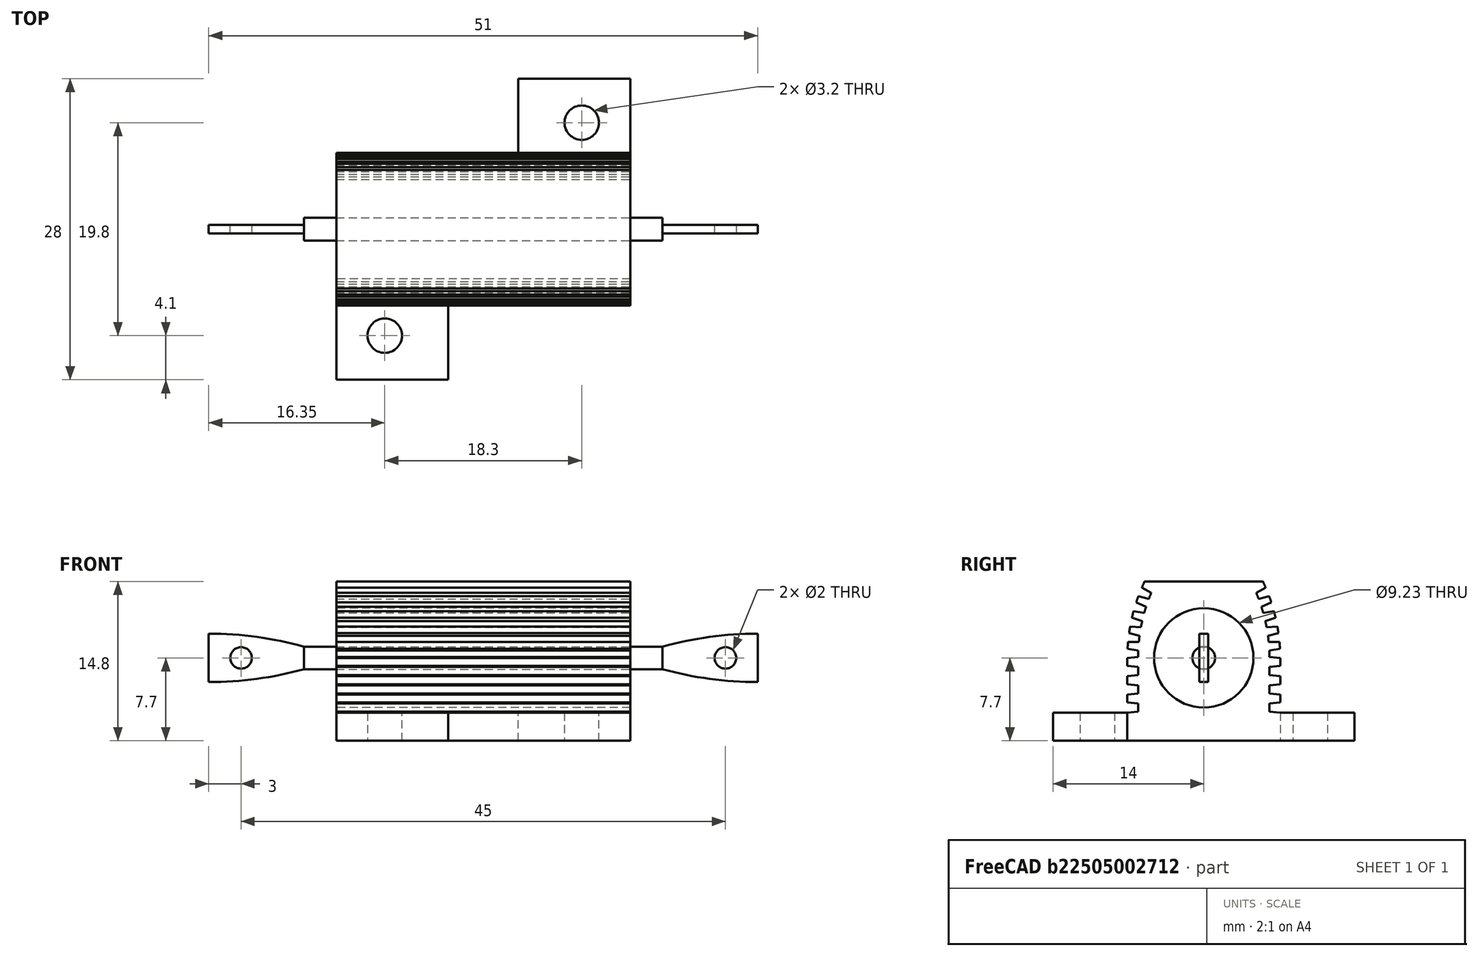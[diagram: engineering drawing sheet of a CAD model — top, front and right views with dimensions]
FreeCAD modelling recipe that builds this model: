
FCSTD DOCUMENT  (FreeCAD 0.20R29410 (Git))
Label: Arcol_HS10-50
License: All rights reserved
LicenseURL: http://en.wikipedia.org/wiki/All_rights_reserved
objects: Sketcher::SketchObject×5, Part::Extrusion×3, Part::Revolution×2, Spreadsheet::Sheet×1, Part::MultiFuse×1, Part::Compound×1
note: 12 computed .brp shape members not serialized (recipe doc carries the construction recipe); baked Part::Feature solids carry a one-line shape summary decoded from their .brp

FEATURE [Spreadsheet::Sheet] Spreadsheet  label="DS"
  cells = A1=A; B1(DS_A)=28; D1=16.5; E1=21; F1=28; G1=28; A2=B; B2(DS_B)=51; D2=30; E2=36.5; F2=51; G2=72.5; A3=C; B3(DS_C)=14.8; D3=8.800000000000001; E3=11; F3=14.8; G3=14.8; A4=D; B4(DS_D)=14.2; D4=8.5; E4=11.2; F4=14.2; G4=14.2; A5=E; B5(DS_E)=27.3; D5=15.9; E5=19.9; F5=27.3; G5=49.1; A6=F; B6(DS_F)=18.3; D6=11.3; E6=14.3; F6=18.3; G6=39.7; A7=G; B7(DS_G)=19.8; D7=12.4; E7=15.9; F7=19.8; G7=21.4; A8=H; B8(DS_H)=7.7; D8=4.5; E8=5.5; F8=7.7; G8=8.4; A9=J; B9(DS_J)=5.2; D9=2.4; E9=2.8; F9=5.2; G9=5.2; A10=K; B10(DS_K)=2.6; D10=1.8; E10=1.8; F10=2.6; G10=2.6; A11=L; B11(DS_L)=3.2; D11=2.4; E11=2.4; F11=3.2; G11=3.2; D13=HS10; E13=HS15; F13=HS25; G13=HS50; A14=Fill_Factor; B14(Fill_Factor)=0.65; A15=Fill_Cone_Height; B15(Fill_Cone_Height)=1; A16=Fill_Cone_Diam; B16(Fill_Cone_Size)=0.65; A17=Fin_Depth; B17(Fin_Depth)=1; A18=Fin_Draft; B18(Fin_Draft)=0.1; A19=Label_Width; B19(Label_Width)=11; A20=Wire_Diam; B20(Wire_Diam)=2.1; A21=Wire_Len; B21(Wire_Len)=3; A22=Con_Thickness; B22(Con_Thickness)=0.8; A23=Con_Width; B23(Con_Width)=4.5; A24=Con_Hole; B24(Con_Hole)=2; A25=Con_Hole_Dist; B25(Con_Hole_Dist)=3
FEATURE [Sketcher::SketchObject] Sketch  label="Sketch_Body_Main"
  FullyConstrained = true
  Placement = pos=(0,0,0) rot=(0.57735,0.57735,0.57735;2.0944rad)
  expr: Constraints[157] = <<DS>>.DS_K
  expr: Constraints[158] = <<DS>>.Fin_Draft
  expr: Constraints[159] = <<DS>>.Fin_Draft
  expr: Constraints[160] = <<DS>>.Fin_Draft
  expr: Constraints[161] = <<DS>>.Fin_Draft
  expr: Constraints[162] = <<DS>>.Fin_Draft
  expr: Constraints[163] = <<DS>>.Fin_Draft
  expr: Constraints[1] = <<DS>>.Label_Width / 2
  expr: Constraints[233] = <<DS>>.DS_D * <<DS>>.Fill_Factor
  expr: Constraints[234] = <<DS>>.DS_H
  expr: Constraints[236] = <<DS>>.Fin_Draft
  expr: Constraints[239] = <<DS>>.Fin_Draft
  expr: Constraints[2] = <<DS>>.DS_C
  expr: Constraints[46] = <<DS>>.Fin_Draft
  expr: Constraints[47] = <<DS>>.Fin_Draft
  expr: Constraints[48] = <<DS>>.Fin_Draft
  expr: Constraints[49] = <<DS>>.Fin_Draft
  expr: Constraints[50] = <<DS>>.Fin_Draft
  expr: Constraints[51] = <<DS>>.Fin_Draft
  expr: Constraints[52] = <<DS>>.Fin_Draft
  expr: Constraints[53] = <<DS>>.Fin_Draft
  expr: Constraints[5] = <<DS>>.DS_D / 2
  expr: Constraints[6] = <<DS>>.DS_H
  expr: Constraints[9] = <<DS>>.Fin_Depth
  sketch-geometry (100):
    g0: LineSegment StartX=-5.5 StartY=14.8 StartZ=0 EndX=5.5 EndY=14.8 EndZ=0
    g1: ArcOfCircle CenterX=-9.45313 CenterY=7.7 CenterZ=0 NormalX=0 NormalY=0 NormalZ=1 AngleXU=0 Radius=16.5531 StartAngle=0 EndAngle=0.443299
    g2: ArcOfCircle CenterX=-9.45313 CenterY=7.7 CenterZ=0 NormalX=0 NormalY=0 NormalZ=1 AngleXU=0 Radius=15.5531 StartAngle=0 EndAngle=0.917514
    g3: LineSegment StartX=-9.45313 StartY=7.7 StartZ=0 EndX=7.0997 EndY=7.8 EndZ=0
    g4: LineSegment StartX=-9.45313 StartY=7.7 StartZ=0 EndX=7.08374 EndY=8.43356 EndZ=0
    g5: LineSegment StartX=-9.45313 StartY=7.7 StartZ=0 EndX=7.079 EndY=8.53345 EndZ=0
    g6: LineSegment StartX=7.03498 StartY=9.16568 StartZ=0 EndX=-9.45313 EndY=7.7 EndZ=0
    g7: LineSegment StartX=-9.45313 StartY=7.7 StartZ=0 EndX=7.02583 EndY=9.26526 EndZ=0
    g8: LineSegment StartX=6.95383 StartY=9.89491 StartZ=0 EndX=-9.45313 EndY=7.7 EndZ=0
    g9: LineSegment StartX=-9.45313 StartY=7.7 StartZ=0 EndX=6.94027 EndY=9.99399 EndZ=0
    g10: LineSegment StartX=6.84045 StartY=10.6198 StartZ=0 EndX=-9.45313 EndY=7.7 EndZ=0
    g11: LineSegment StartX=6.82251 StartY=10.7182 StartZ=0 EndX=-9.45313 EndY=7.7 EndZ=0
    g12: LineSegment StartX=6.67277 StartY=11.4365 StartZ=0 EndX=-9.45313 EndY=7.7 EndZ=0
    g13: LineSegment StartX=6.69505 StartY=11.339 StartZ=0 EndX=-9.45313 EndY=7.7 EndZ=0
    g14: LineSegment StartX=6.51792 StartY=12.0511 StartZ=0 EndX=-9.45313 EndY=7.7 EndZ=0
    g15: LineSegment StartX=6.49134 StartY=12.1475 StartZ=0 EndX=-9.45313 EndY=7.7 EndZ=0
    g16: LineSegment StartX=6.30941 StartY=12.7546 StartZ=0 EndX=-9.45313 EndY=7.7 EndZ=0
    g17: LineSegment StartX=6.27859 StartY=12.8497 StartZ=0 EndX=-9.45313 EndY=7.7 EndZ=0
    g18: LineSegment StartX=6.03492 StartY=13.5418 StartZ=0 EndX=-9.45313 EndY=7.7 EndZ=0
    g19: LineSegment StartX=6.06993 StartY=13.4481 StartZ=0 EndX=-9.45313 EndY=7.7 EndZ=0
    g20: LineSegment StartX=5.79995 StartY=14.1304 StartZ=0 EndX=-9.45313 EndY=7.7 EndZ=0
    g21: LineSegment StartX=6.30941 StartY=12.7546 StartZ=0 EndX=6.49134 EndY=12.1475 EndZ=0
    g22: LineSegment StartX=6.84045 StartY=10.6198 StartZ=0 EndX=6.94027 EndY=9.99399 EndZ=0
    g23: LineSegment StartX=6.95383 StartY=9.89491 StartZ=0 EndX=7.02583 EndY=9.26526 EndZ=0
    g24: LineSegment StartX=7.03498 StartY=9.16568 StartZ=0 EndX=7.079 EndY=8.53345 EndZ=0
    g25: LineSegment StartX=7.08374 StartY=8.43356 StartZ=0 EndX=7.0997 EndY=7.8 EndZ=0
    g26: LineSegment StartX=7.1 StartY=7.7 StartZ=0 EndX=6.09972 EndY=7.79396 EndZ=0
    g27: LineSegment StartX=6.08472 StartY=8.38924 StartZ=0 EndX=7.079 EndY=8.53345 EndZ=0
    g28: LineSegment StartX=7.03498 StartY=9.16568 StartZ=0 EndX=6.03031 EndY=9.1707 EndZ=0
    g29: LineSegment StartX=5.96266 StartY=9.76231 StartZ=0 EndX=6.94027 EndY=9.99399 EndZ=0
    g30: LineSegment StartX=6.84045 StartY=10.6198 StartZ=0 EndX=5.83927 EndY=10.5359 EndZ=0
    g31: LineSegment StartX=5.71951 StartY=11.1192 StartZ=0 EndX=6.67277 EndY=11.4365 EndZ=0
    g32: LineSegment StartX=6.51792 StartY=12.0511 StartZ=0 EndX=5.52811 EndY=11.8788 EndZ=0
    g33: LineSegment StartX=5.35717 StartY=12.4492 StartZ=0 EndX=6.27859 EndY=12.8497 EndZ=0
    g34: LineSegment StartX=6.06993 StartY=13.4481 StartZ=0 EndX=5.09926 EndY=13.1889 EndZ=0
    g35: ArcOfCircle CenterX=-9.45313 CenterY=7.7 CenterZ=0 NormalX=0 NormalY=0 NormalZ=1 AngleXU=0 Radius=15.5531 StartAngle=0.00604116 EndAngle=0.0443299
    g36: ArcOfCircle CenterX=-9.45313 CenterY=7.7 CenterZ=0 NormalX=0 NormalY=0 NormalZ=1 AngleXU=0 Radius=16.5531 StartAngle=0.0503711 EndAngle=0.0886598
    g37: ArcOfCircle CenterX=-9.45313 CenterY=7.7 CenterZ=0 NormalX=0 NormalY=0 NormalZ=1 AngleXU=0 Radius=15.5531 StartAngle=0.094701 EndAngle=0.13299
    g38: ArcOfCircle CenterX=-9.45313 CenterY=7.7 CenterZ=0 NormalX=0 NormalY=0 NormalZ=1 AngleXU=0 Radius=16.5531 StartAngle=0.139031 EndAngle=0.17732
    g39: ArcOfCircle CenterX=-9.45313 CenterY=7.7 CenterZ=0 NormalX=0 NormalY=0 NormalZ=1 AngleXU=0 Radius=15.5531 StartAngle=0.183361 EndAngle=0.22165
    g40: ArcOfCircle CenterX=-9.45313 CenterY=7.7 CenterZ=0 NormalX=0 NormalY=0 NormalZ=1 AngleXU=0 Radius=16.5531 StartAngle=0.227691 EndAngle=0.265979
    g41: ArcOfCircle CenterX=-9.45313 CenterY=7.7 CenterZ=0 NormalX=0 NormalY=0 NormalZ=1 AngleXU=0 Radius=15.5531 StartAngle=0.272021 EndAngle=0.310309
    g42: ArcOfCircle CenterX=-9.45313 CenterY=7.7 CenterZ=0 NormalX=0 NormalY=0 NormalZ=1 AngleXU=0 Radius=16.5531 StartAngle=0.316351 EndAngle=0.354639
    g43: ArcOfCircle CenterX=-9.45313 CenterY=7.7 CenterZ=0 NormalX=0 NormalY=0 NormalZ=1 AngleXU=0 Radius=15.5531 StartAngle=0.36068 EndAngle=0.398969
    g44: LineSegment StartX=7.1 StartY=7.7 StartZ=0 EndX=7.1 EndY=6.95 EndZ=0
    g45: LineSegment StartX=7.1 StartY=6.95 StartZ=0 EndX=6.1 EndY=6.85 EndZ=0
    g46: LineSegment StartX=6.1 StartY=6.85 StartZ=0 EndX=6.1 EndY=6.1 EndZ=0
    g47: LineSegment StartX=6.1 StartY=6.1 StartZ=0 EndX=7.1 EndY=6 EndZ=0
    g48: LineSegment StartX=7.1 StartY=6 StartZ=0 EndX=7.1 EndY=5.25 EndZ=0
    g49: LineSegment StartX=7.1 StartY=5.25 StartZ=0 EndX=6.1 EndY=5.15 EndZ=0
    g50: LineSegment StartX=6.1 StartY=5.15 StartZ=0 EndX=6.1 EndY=4.4 EndZ=0
    g51: LineSegment StartX=6.1 StartY=4.4 StartZ=0 EndX=7.1 EndY=4.3 EndZ=0
    g52: LineSegment StartX=7.1 StartY=4.3 StartZ=0 EndX=7.1 EndY=3.55 EndZ=0
    g53: LineSegment StartX=7.1 StartY=3.55 StartZ=0 EndX=6.1 EndY=3.45 EndZ=0
    g54: LineSegment StartX=6.1 StartY=3.45 StartZ=0 EndX=6.1 EndY=2.7 EndZ=0
    g55: LineSegment StartX=6.1 StartY=2.7 StartZ=0 EndX=7.1 EndY=2.6 EndZ=0
    g56: LineSegment StartX=7.1 StartY=2.6 StartZ=0 EndX=7.1 EndY=0 EndZ=0
    g57: LineSegment StartX=7.1 StartY=0 StartZ=0 EndX=-7.1 EndY=0 EndZ=0
    g58: LineSegment StartX=-7.1 StartY=0 StartZ=0 EndX=-7.1 EndY=2.6 EndZ=0
    g59: LineSegment StartX=-7.1 StartY=2.6 StartZ=0 EndX=-6.1 EndY=2.7 EndZ=0
    g60: LineSegment StartX=-6.1 StartY=2.7 StartZ=0 EndX=-6.1 EndY=3.45 EndZ=0
    g61: LineSegment StartX=-6.1 StartY=3.45 StartZ=0 EndX=-7.1 EndY=3.55 EndZ=0
    g62: LineSegment StartX=-7.1 StartY=3.55 StartZ=0 EndX=-7.1 EndY=4.3 EndZ=0
    g63: LineSegment StartX=-7.1 StartY=4.3 StartZ=0 EndX=-6.1 EndY=4.4 EndZ=0
    g64: LineSegment StartX=-6.1 StartY=4.4 StartZ=0 EndX=-6.1 EndY=5.15 EndZ=0
    g65: LineSegment StartX=-6.1 StartY=5.15 StartZ=0 EndX=-7.1 EndY=5.25 EndZ=0
    g66: LineSegment StartX=-7.1 StartY=5.25 StartZ=0 EndX=-7.1 EndY=6 EndZ=0
    g67: LineSegment StartX=-7.1 StartY=6 StartZ=0 EndX=-6.1 EndY=6.1 EndZ=0
    g68: LineSegment StartX=-6.1 StartY=6.1 StartZ=0 EndX=-6.1 EndY=6.85 EndZ=0
    g69: LineSegment StartX=-6.1 StartY=6.85 StartZ=0 EndX=-7.1 EndY=6.95 EndZ=0
    g70: LineSegment StartX=-7.1 StartY=6.95 StartZ=0 EndX=-7.1 EndY=7.7 EndZ=0
    g71: LineSegment StartX=-7.1 StartY=7.7 StartZ=0 EndX=-6.09972 EndY=7.79396 EndZ=0
    g72: LineSegment StartX=-6.08472 StartY=8.38924 StartZ=0 EndX=-7.079 EndY=8.53345 EndZ=0
    g73: LineSegment StartX=-7.03498 StartY=9.16568 StartZ=0 EndX=-6.03031 EndY=9.1707 EndZ=0
    g74: LineSegment StartX=-5.96266 StartY=9.76231 StartZ=0 EndX=-6.94027 EndY=9.99399 EndZ=0
    g75: LineSegment StartX=-6.84045 StartY=10.6198 StartZ=0 EndX=-5.83927 EndY=10.5359 EndZ=0
    g76: LineSegment StartX=-5.71951 StartY=11.1192 StartZ=0 EndX=-6.67277 EndY=11.4365 EndZ=0
    g77: LineSegment StartX=-6.51792 StartY=12.0511 StartZ=0 EndX=-5.52811 EndY=11.8788 EndZ=0
    g78: LineSegment StartX=-5.35717 StartY=12.4492 StartZ=0 EndX=-6.27859 EndY=12.8497 EndZ=0
    g79: LineSegment StartX=-6.06993 StartY=13.4481 StartZ=0 EndX=-5.09926 EndY=13.1889 EndZ=0
    g80: ArcOfCircle CenterX=9.45313 CenterY=7.7 CenterZ=0 NormalX=0 NormalY=0 NormalZ=1 AngleXU=0 Radius=15.5531 StartAngle=3.09726 EndAngle=3.13555
    g81: ArcOfCircle CenterX=9.45313 CenterY=7.7 CenterZ=0 NormalX=0 NormalY=0 NormalZ=1 AngleXU=0 Radius=16.5531 StartAngle=3.05293 EndAngle=3.09122
    g82: ArcOfCircle CenterX=9.45313 CenterY=7.7 CenterZ=0 NormalX=0 NormalY=0 NormalZ=1 AngleXU=0 Radius=15.5531 StartAngle=3.0086 EndAngle=3.04689
    g83: ArcOfCircle CenterX=9.45313 CenterY=7.7 CenterZ=0 NormalX=0 NormalY=0 NormalZ=1 AngleXU=0 Radius=16.5531 StartAngle=2.96427 EndAngle=3.00256
    g84: ArcOfCircle CenterX=9.45313 CenterY=7.7 CenterZ=0 NormalX=0 NormalY=0 NormalZ=1 AngleXU=0 Radius=15.5531 StartAngle=2.91994 EndAngle=2.95823
    g85: ArcOfCircle CenterX=9.45313 CenterY=7.7 CenterZ=0 NormalX=0 NormalY=0 NormalZ=1 AngleXU=0 Radius=16.5531 StartAngle=2.87561 EndAngle=2.9139
    g86: ArcOfCircle CenterX=9.45313 CenterY=7.7 CenterZ=0 NormalX=0 NormalY=0 NormalZ=1 AngleXU=0 Radius=15.5531 StartAngle=2.83128 EndAngle=2.86957
    g87: ArcOfCircle CenterX=9.45313 CenterY=7.7 CenterZ=0 NormalX=0 NormalY=0 NormalZ=1 AngleXU=0 Radius=16.5531 StartAngle=2.78695 EndAngle=2.82524
    g88: ArcOfCircle CenterX=9.45313 CenterY=7.7 CenterZ=0 NormalX=0 NormalY=0 NormalZ=1 AngleXU=0 Radius=15.5531 StartAngle=2.74262 EndAngle=2.78091
    g89: Circle CenterX=0 CenterY=7.7 CenterZ=0 NormalX=0 NormalY=0 NormalZ=1 AngleXU=0 Radius=4.615
    g90: LineSegment StartX=-9.45313 StartY=7.7 StartZ=0 EndX=5.76082 EndY=14.2224 EndZ=0
    g91: LineSegment StartX=4.87849 StartY=13.7419 StartZ=0 EndX=5.76082 EndY=14.2224 EndZ=0
    g92: ArcOfCircle CenterX=-9.45313 CenterY=7.7 CenterZ=0 NormalX=0 NormalY=0 NormalZ=1 AngleXU=0 Radius=16.5531 StartAngle=0.40501 EndAngle=0.443299
    g93: LineSegment StartX=6.69505 StartY=11.339 StartZ=0 EndX=6.82251 EndY=10.7182 EndZ=0
    g94: LineSegment StartX=6.03492 StartY=13.5418 StartZ=0 EndX=5.79995 EndY=14.1304 EndZ=0
    g95: LineSegment StartX=6.06993 StartY=13.4481 StartZ=0 EndX=6.27859 EndY=12.8497 EndZ=0
    g96: LineSegment StartX=6.51792 StartY=12.0511 StartZ=0 EndX=6.67277 EndY=11.4365 EndZ=0
    g97: LineSegment StartX=5.5 StartY=14.8 StartZ=0 EndX=5.76082 EndY=14.2224 EndZ=0
    g98: LineSegment StartX=-4.87849 StartY=13.7419 StartZ=0 EndX=-5.76082 EndY=14.2224 EndZ=0
    g99: ArcOfCircle CenterX=9.45313 CenterY=7.7 CenterZ=0 NormalX=0 NormalY=0 NormalZ=1 AngleXU=0 Radius=16.5531 StartAngle=2.69829 EndAngle=2.73658
  constraints (268):
    c: Symmetric(g0,g0,g-2)
    c: Distance(g0,g-2) = 5.5
    c: Distance(g0,g-1) = 14.8
    c: Coincident(g0,g1)
    c: DistanceY(g1,g1) = 0
    c: Distance(g1,g-2) = 7.1
    c: Distance(g1,g-1) = 7.7
    c: Coincident(g2,g1)
    c: DistanceY(g1,g2) = 0
    c: Distance(g2,g1) = 1
    c: Coincident(g3,g1)
    c: PointOnObject(g3,g1)
    c: Coincident(g4,g1)
    c: PointOnObject(g4,g1)
    c: Coincident(g5,g1)
    c: PointOnObject(g5,g1)
    c: PointOnObject(g6,g1)
    c: Coincident(g6,g1)
    c: Coincident(g7,g1)
    c: PointOnObject(g7,g1)
    c: PointOnObject(g8,g1)
    c: Coincident(g8,g1)
    c: Coincident(g9,g1)
    c: PointOnObject(g9,g1)
    c: PointOnObject(g10,g1)
    c: Coincident(g10,g1)
    c: PointOnObject(g11,g1)
    c: Coincident(g11,g1)
    c: PointOnObject(g12,g1)
    c: Coincident(g12,g1)
    c: PointOnObject(g13,g1)
    c: Coincident(g13,g1)
    c: PointOnObject(g14,g1)
    c: Coincident(g14,g1)
    c: PointOnObject(g15,g1)
    c: Coincident(g15,g1)
    c: PointOnObject(g16,g1)
    c: Coincident(g16,g1)
    c: PointOnObject(g17,g1)
    c: Coincident(g17,g1)
    c: PointOnObject(g18,g1)
    c: Coincident(g18,g1)
    c: PointOnObject(g19,g1)
    c: Coincident(g19,g1)
    c: PointOnObject(g20,g1)
    c: Coincident(g20,g1)
    c: Distance(g4,g5) = 0.1
    c: Distance(g6,g7) = 0.1
    c: Distance(g8,g9) = 0.1
    c: Distance(g10,g11) = 0.1
    c: Distance(g12,g13) = 0.1
    c: Distance(g14,g15) = 0.1
    c: Distance(g16,g17) = 0.1
    c: Distance(g18,g19) = 0.1
    c: Coincident(g25,g3)
    c: Coincident(g25,g4)
    c: Coincident(g24,g5)
    c: Coincident(g6,g24)
    c: Coincident(g7,g23)
    c: Coincident(g23,g8)
    c: Coincident(g22,g9)
    c: Coincident(g22,g10)
    c: Coincident(g15,g21)
    c: Coincident(g21,g16)
    c: Equal(g22,g23)
    c: Equal(g23,g24)
    c: Equal(g24,g25)
    c: Coincident(g26,g1)
    c: PointOnObject(g26,g3)
    c: PointOnObject(g26,g2)
    c: PointOnObject(g27,g4)
    c: Coincident(g27,g5)
    c: Coincident(g28,g6)
    c: PointOnObject(g28,g7)
    c: PointOnObject(g29,g8)
    c: Coincident(g29,g9)
    c: Coincident(g30,g10)
    c: PointOnObject(g30,g11)
    c: PointOnObject(g31,g13)
    c: Coincident(g31,g12)
    c: Coincident(g32,g14)
    c: PointOnObject(g32,g15)
    c: PointOnObject(g33,g16)
    c: Coincident(g33,g17)
    c: Coincident(g34,g19)
    c: PointOnObject(g34,g18)
    c: PointOnObject(g27,g2)
    c: PointOnObject(g28,g2)
    c: PointOnObject(g29,g2)
    c: PointOnObject(g30,g2)
    c: PointOnObject(g31,g2)
    c: PointOnObject(g32,g2)
    c: PointOnObject(g33,g2)
    c: PointOnObject(g34,g2)
    c: Coincident(g35,g1)
    c: Coincident(g35,g26)
    c: PointOnObject(g35,g4)
    c: Coincident(g36,g35)
    c: Coincident(g36,g27)
    c: PointOnObject(g36,g6)
    c: Coincident(g37,g35)
    c: Coincident(g37,g28)
    c: PointOnObject(g37,g8)
    c: Coincident(g38,g35)
    c: Coincident(g38,g29)
    c: PointOnObject(g38,g10)
    c: Coincident(g39,g35)
    c: Coincident(g39,g30)
    c: PointOnObject(g39,g13)
    c: Coincident(g40,g35)
    c: Coincident(g40,g31)
    c: PointOnObject(g40,g14)
    c: Coincident(g41,g35)
    c: Coincident(g41,g32)
    c: PointOnObject(g41,g16)
    c: Coincident(g42,g35)
    c: Coincident(g42,g33)
    c: PointOnObject(g42,g19)
    c: Coincident(g43,g35)
    c: Coincident(g43,g34)
    c: PointOnObject(g43,g20)
    c: Coincident(g26,g44)
    c: Vertical(g44)
    c: Coincident(g44,g45)
    c: Coincident(g45,g46)
    c: Vertical(g46)
    c: Coincident(g46,g47)
    c: Coincident(g47,g48)
    c: Vertical(g48)
    c: Coincident(g48,g49)
    c: Coincident(g49,g50)
    c: Vertical(g50)
    c: Coincident(g50,g51)
    c: Coincident(g51,g52)
    c: Vertical(g52)
    c: Coincident(g52,g53)
    c: Coincident(g53,g54)
    c: Vertical(g54)
    c: Coincident(g54,g55)
    c: Coincident(g55,g56)
    c: PointOnObject(g56,g-1)
    c: Vertical(g56)
    c: Coincident(g56,g57)
    c: Coincident(g57,g58)
    c: Coincident(g58,g59)
    c: Coincident(g59,g60)
    c: Coincident(g60,g61)
    c: Coincident(g61,g62)
    c: Coincident(g62,g63)
    c: Coincident(g63,g64)
    c: Coincident(g64,g65)
    c: Coincident(g65,g66)
    c: Coincident(g66,g67)
    c: Coincident(g67,g68)
    c: Coincident(g68,g69)
    c: Coincident(g69,g70)
    c: Symmetric(g56,g57,g-2)
    c: Distance(g56) = 2.6
    c: DistanceY(g55,g54) = 0.1
    c: DistanceY(g53,g52) = 0.1
    c: DistanceY(g51,g50) = 0.1
    c: DistanceY(g49,g48) = 0.1
    c: DistanceY(g47,g46) = 0.1
    c: DistanceY(g45,g44) = 0.1
    c: DistanceX(g47,g44) = 0
    c: DistanceX(g51,g48) = 0
    c: DistanceX(g55,g52) = 0
    c: DistanceX(g2,g45) = 0
    c: DistanceX(g46,g49) = 0
    c: DistanceX(g50,g53) = 0
    c: Equal(g44,g46)
    c: Equal(g46,g48)
    c: Equal(g48,g50)
    c: Equal(g50,g52)
    c: Equal(g52,g54)
    c: Symmetric(g58,g55,g-2)
    c: Symmetric(g59,g54,g-2)
    c: Symmetric(g60,g53,g-2)
    c: Symmetric(g61,g52,g-2)
    c: Symmetric(g62,g51,g-2)
    c: Symmetric(g63,g50,g-2)
    c: Symmetric(g64,g49,g-2)
    c: Symmetric(g65,g48,g-2)
    c: Symmetric(g66,g47,g-2)
    c: Symmetric(g67,g46,g-2)
    c: Symmetric(g68,g45,g-2)
    c: Symmetric(g69,g44,g-2)
    c: Symmetric(g70,g26,g-2)
    c: Coincident(g71,g70)
    c: Symmetric(g71,g26,g-2)
    c: Symmetric(g72,g27,g-2)
    c: Symmetric(g72,g27,g-2)
    c: Symmetric(g73,g28,g-2)
    c: Symmetric(g73,g28,g-2)
    c: Symmetric(g74,g29,g-2)
    c: Symmetric(g74,g29,g-2)
    c: Symmetric(g75,g30,g-2)
    c: Symmetric(g75,g30,g-2)
    c: Symmetric(g76,g31,g-2)
    c: Symmetric(g76,g31,g-2)
    c: Symmetric(g77,g32,g-2)
    c: Symmetric(g77,g32,g-2)
    c: Symmetric(g78,g33,g-2)
    c: Symmetric(g78,g33,g-2)
    c: Symmetric(g79,g34,g-2)
    c: Symmetric(g79,g34,g-2)
    c: Coincident(g80,g71)
    c: PointOnObject(g80,g72)
    c: Symmetric(g80,g35,g-2)
    c: Coincident(g81,g80)
    c: Coincident(g81,g72)
    c: PointOnObject(g81,g73)
    c: Coincident(g82,g80)
    c: Coincident(g82,g73)
    c: PointOnObject(g82,g74)
    c: Coincident(g83,g80)
    c: Coincident(g83,g74)
    c: PointOnObject(g83,g75)
    c: Coincident(g84,g80)
    c: Coincident(g84,g75)
    c: PointOnObject(g84,g76)
    c: Coincident(g85,g80)
    c: Coincident(g85,g76)
    c: PointOnObject(g85,g77)
    c: Coincident(g86,g80)
    c: Coincident(g86,g77)
    c: PointOnObject(g86,g78)
    c: Coincident(g87,g80)
    c: Coincident(g87,g78)
    c: PointOnObject(g87,g79)
    c: Coincident(g88,g80)
    c: PointOnObject(g88,g79)
    c: PointOnObject(g2,g-2)
    c: Diameter(g89) = 9.23
    c: Distance(g89,g-1) = 7.7
    c: PointOnObject(g89,g-2)
    c: Distance(g3,g26) = 0.1
    c: Coincident(g90,g35)
    c: PointOnObject(g90,g1)
    c: Distance(g90,g20) = 0.1
    c: PointOnObject(g91,g2)
    c: Coincident(g91,g90)
    c: PointOnObject(g91,g20)
    c: Coincident(g92,g35)
    c: Coincident(g92,g91)
    c: PointOnObject(g92,g0)
    c: Coincident(g93,g13)
    c: Coincident(g93,g11)
    c: Coincident(g94,g18)
    c: Coincident(g94,g20)
    c: Coincident(g95,g34)
    c: Coincident(g95,g33)
    c: Equal(g94,g95)
    c: Equal(g95,g21)
    c: Coincident(g96,g32)
    c: Coincident(g96,g31)
    c: Equal(g96,g21)
    c: Equal(g93,g21)
    c: Equal(g23,g93)
    c: Symmetric(g43,g88,g-2)
    c: Coincident(g97,g0)
    c: Coincident(g97,g91)
    c: Equal(g94,g97)
    c: Coincident(g98,g88)
    c: Coincident(g99,g98)
    c: Symmetric(g99,g35,g-2)
    c: PointOnObject(g99,g0)
    c: Symmetric(g98,g91,g-2)
FEATURE [Part::Extrusion] Extrude  label="Body Main"
  Base = -> Sketch
  Dir = (1,0,0)
  DirMode = 2
  FaceMakerClass = Part::FaceMakerBullseye
  LengthFwd = 27.3
  LengthRev = 0
  Solid = true
  Symmetric = true
  expr: LengthFwd = <<DS>>.DS_E
FEATURE [Sketcher::SketchObject] Sketch001  label="Sketch_Body_Mount"
  FullyConstrained = true
  expr: Constraints[10] = <<DS>>.DS_E / 2
  expr: Constraints[11] = <<DS>>.DS_A / 2
  expr: Constraints[20] = <<DS>>.DS_J * 2
  expr: Constraints[21] = (<<DS>>.DS_A - <<DS>>.DS_D) / 2
  expr: Constraints[22] = <<DS>>.DS_A / 2
  expr: Constraints[23] = <<DS>>.DS_E / 2
  expr: Constraints[24] = <<DS>>.DS_L
  expr: Constraints[25] = <<DS>>.DS_L
  expr: Constraints[26] = <<DS>>.DS_G / 2
  expr: Constraints[27] = <<DS>>.DS_G / 2
  expr: Constraints[28] = <<DS>>.DS_F / 2
  expr: Constraints[29] = <<DS>>.DS_F / 2
  expr: Constraints[8] = <<DS>>.DS_J * 2
  expr: Constraints[9] = (<<DS>>.DS_A - <<DS>>.DS_D) / 2
  sketch-geometry (10):
    g0: LineSegment StartX=13.65 StartY=14 StartZ=0 EndX=3.25 EndY=14 EndZ=0
    g1: LineSegment StartX=3.25 StartY=14 StartZ=0 EndX=3.25 EndY=7.1 EndZ=0
    g2: LineSegment StartX=3.25 StartY=7.1 StartZ=0 EndX=13.65 EndY=7.1 EndZ=0
    g3: LineSegment StartX=13.65 StartY=7.1 StartZ=0 EndX=13.65 EndY=14 EndZ=0
    g4: LineSegment StartX=-13.65 StartY=-14 StartZ=0 EndX=-3.25 EndY=-14 EndZ=0
    g5: LineSegment StartX=-3.25 StartY=-14 StartZ=0 EndX=-3.25 EndY=-7.1 EndZ=0
    g6: LineSegment StartX=-3.25 StartY=-7.1 StartZ=0 EndX=-13.65 EndY=-7.1 EndZ=0
    g7: LineSegment StartX=-13.65 StartY=-7.1 StartZ=0 EndX=-13.65 EndY=-14 EndZ=0
    g8: Circle CenterX=9.15 CenterY=9.9 CenterZ=0 NormalX=0 NormalY=0 NormalZ=1 AngleXU=0 Radius=1.6
    g9: Circle CenterX=-9.15 CenterY=-9.9 CenterZ=0 NormalX=0 NormalY=0 NormalZ=1 AngleXU=0 Radius=1.6
  constraints (30):
    c: Coincident(g0,g1)
    c: Coincident(g1,g2)
    c: Coincident(g2,g3)
    c: Coincident(g3,g0)
    c: Horizontal(g0)
    c: Horizontal(g2)
    c: Vertical(g1)
    c: Vertical(g3)
    c: Distance(g1,g2) = 10.4
    c: Distance(g2,g0) = 6.9
    c: Distance(g0,g-2) = 13.65
    c: Distance(g0,g-1) = 14
    c: Coincident(g4,g5)
    c: Coincident(g5,g6)
    c: Coincident(g6,g7)
    c: Coincident(g7,g4)
    c: Horizontal(g4)
    c: Horizontal(g6)
    c: Vertical(g5)
    c: Vertical(g7)
    c: Distance(g4,g4) = 10.4
    c: Distance(g4,g6) = 6.9
    c: Distance(g4,g-1) = 14
    c: Distance(g4,g-2) = 13.65
    c: Diameter(g8) = 3.2
    c: Diameter(g9) = 3.2
    c: Distance(g8,g-1) = 9.9
    c: Distance(g9,g-1) = 9.9
    c: Distance(g8,g-2) = 9.15
    c: Distance(g9,g-2) = 9.15
FEATURE [Part::Extrusion] Extrude001  label="Body Mount"
  Base = -> Sketch001
  Dir = (0,0,1)
  DirMode = 2
  FaceMakerClass = Part::FaceMakerBullseye
  LengthFwd = 2.6
  LengthRev = 0
  Solid = true
  Symmetric = false
  expr: LengthFwd = <<DS>>.DS_K
FEATURE [Part::MultiFuse] Fusion  label="Body"
  Shapes = -> [Extrude001,Extrude]
FEATURE [Sketcher::SketchObject] Sketch002  label="Sketch_Fill"
  FullyConstrained = true
  expr: .Placement.Base.z = 0
  expr: Constraints[12] = <<DS>>.DS_D * <<DS>>.Fill_Factor * <<DS>>.Fill_Cone_Size / 2
  expr: Constraints[17] = <<DS>>.DS_E / 2
  expr: Constraints[19] = <<DS>>.Wire_Diam / 2
  expr: Constraints[1] = <<DS>>.DS_D * <<DS>>.Fill_Factor / 2
  expr: Constraints[2] = <<DS>>.DS_E / 2 - <<DS>>.Fill_Cone_Height
  expr: Constraints[8] = <<DS>>.DS_E / 2
  sketch-geometry (8):
    g0: LineSegment StartX=-12.65 StartY=4.615 StartZ=0 EndX=12.65 EndY=4.615 EndZ=0
    g1: LineSegment StartX=12.65 StartY=4.615 StartZ=0 EndX=12.65 EndY=2.99975 EndZ=0
    g2: LineSegment StartX=-12.65 StartY=4.615 StartZ=0 EndX=-12.65 EndY=2.99975 EndZ=0
    g3: LineSegment StartX=-13.65 StartY=4.615 StartZ=0 EndX=-13.65 EndY=1.05 EndZ=0
    g4: LineSegment StartX=13.65 StartY=4.615 StartZ=0 EndX=13.65 EndY=1.05 EndZ=0
    g5: ArcOfCircle CenterX=11.2492 CenterY=1.05 CenterZ=0 NormalX=0 NormalY=0 NormalZ=1 AngleXU=0 Radius=2.40076 StartAngle=0 EndAngle=0.947807
    g6: ArcOfCircle CenterX=-11.2492 CenterY=1.05 CenterZ=0 NormalX=0 NormalY=0 NormalZ=1 AngleXU=0 Radius=2.40076 StartAngle=2.19379 EndAngle=3.14159
    g7: LineSegment StartX=-13.65 StartY=1.05 StartZ=0 EndX=13.65 EndY=1.05 EndZ=0
  constraints (24):
    c: Symmetric(g0,g0,g-2)
    c: Distance(g0,g-1) = 4.615
    c: Distance(g0,g-2) = 12.65
    c: Coincident(g1,g0)
    c: Coincident(g2,g0)
    c: Vertical(g4)
    c: Symmetric(g3,g4,g-2)
    c: Symmetric(g4,g3,g-2)
    c: Distance(g4,g-2) = 13.65
    c: PointOnObject(g4,g0)
    c: Symmetric(g1,g2,g-2)
    c: Symmetric(g5,g6,g-2)
    c: Distance(g1,g-1) = 2.99975
    c: Coincident(g5,g1)
    c: Coincident(g6,g2)
    c: Tangent(g5,g4)
    c: Vertical(g1)
    c: Distance(g7,g-2) = 13.65
    c: Symmetric(g7,g7,g-2)
    c: Distance(g7,g-1) = 1.05
    c: PointOnObject(g5,g7)
    c: PointOnObject(g4,g7)
    c: PointOnObject(g5,g7)
    c: PointOnObject(g6,g7)
FEATURE [Part::Revolution] Revolve  label="Fill"
  Angle = 360
  Axis = (1,0,0)
  Base = (0,0,0)
  FaceMakerClass = Part::FaceMakerBullseye
  Placement = pos=(0,0,7.7) rot=(0,0,1;0rad)
  Solid = false
  Source = -> Sketch002
  Symmetric = false
  expr: .Placement.Base.z = <<DS>>.DS_H
FEATURE [Sketcher::SketchObject] Sketch003  label="Sketch_Wire"
  FullyConstrained = true
  Placement = pos=(0,0,7.7) rot=(0,0,1;0rad)
  expr: Constraints[10] = <<DS>>.DS_E / 2 + <<DS>>.Wire_Len
  expr: Constraints[11] = <<DS>>.DS_E / 2 + <<DS>>.Wire_Len
  expr: Constraints[9] = <<DS>>.Wire_Diam / 2
  sketch-geometry (4):
    g0: LineSegment StartX=-16.65 StartY=1.05 StartZ=0 EndX=16.65 EndY=1.05 EndZ=0
    g1: LineSegment StartX=16.65 StartY=1.05 StartZ=0 EndX=16.65 EndY=0 EndZ=0
    g2: LineSegment StartX=16.65 StartY=0 StartZ=0 EndX=-16.65 EndY=0 EndZ=0
    g3: LineSegment StartX=-16.65 StartY=0 StartZ=0 EndX=-16.65 EndY=1.05 EndZ=0
  constraints (12):
    c: Coincident(g0,g1)
    c: Coincident(g1,g2)
    c: Coincident(g2,g3)
    c: Coincident(g3,g0)
    c: Horizontal(g0)
    c: Horizontal(g2)
    c: Vertical(g1)
    c: Vertical(g3)
    c: PointOnObject(g1,g-1)
    c: Distance(g0,g-1) = 1.05
    c: Distance(g0,g-2) = 16.65
    c: Distance(g0,g-2) = 16.65
FEATURE [Part::Revolution] Revolve001  label="Wire"
  Angle = 360
  Axis = (1,0,0)
  Base = (0,0,7.7)
  FaceMakerClass = Part::FaceMakerBullseye
  Solid = true
  Source = -> Sketch003
  Symmetric = false
  expr: .Base.z = <<DS>>.DS_H
FEATURE [Sketcher::SketchObject] Sketch004  label="Sketch_Con"
  FullyConstrained = true
  Placement = pos=(0,0,0) rot=(1,0,0;1.5708rad)
  expr: Constraints[10] = <<DS>>.Con_Hole
  expr: Constraints[11] = <<DS>>.Con_Width
  expr: Constraints[14] = <<DS>>.DS_H
  expr: Constraints[15] = <<DS>>.DS_H - <<DS>>.Con_Width / 2
  expr: Constraints[17] = <<DS>>.Con_Hole
  expr: Constraints[28] = <<DS>>.Con_Hole_Dist
  expr: Constraints[6] = <<DS>>.DS_H + <<DS>>.Wire_Diam / 2
  expr: Constraints[7] = <<DS>>.DS_H - <<DS>>.Wire_Diam / 2
  expr: Constraints[8] = <<DS>>.DS_E / 2 + <<DS>>.Wire_Len
  expr: Constraints[9] = <<DS>>.DS_B / 2
  sketch-geometry (10):
    g0: Circle CenterX=22.5 CenterY=7.7 CenterZ=0 NormalX=0 NormalY=0 NormalZ=1 AngleXU=0 Radius=1
    g1: LineSegment StartX=16.65 StartY=8.75 StartZ=0 EndX=16.65 EndY=6.65 EndZ=0
    g2: ArcOfCircle CenterX=25.5 CenterY=-23.2844 CenterZ=0 NormalX=0 NormalY=0 NormalZ=1 AngleXU=0 Radius=33.2344 StartAngle=1.5708 EndAngle=1.84034
    g3: ArcOfCircle CenterX=25.5 CenterY=38.6844 CenterZ=0 NormalX=0 NormalY=0 NormalZ=1 AngleXU=0 Radius=33.2344 StartAngle=4.44285 EndAngle=4.71239
    g4: LineSegment StartX=25.5 StartY=9.95 StartZ=0 EndX=25.5 EndY=5.45 EndZ=0
    g5: Circle CenterX=-22.5 CenterY=7.7 CenterZ=0 NormalX=0 NormalY=0 NormalZ=1 AngleXU=0 Radius=1
    g6: ArcOfCircle CenterX=-25.5 CenterY=-23.2844 CenterZ=0 NormalX=0 NormalY=0 NormalZ=1 AngleXU=0 Radius=33.2344 StartAngle=1.30125 EndAngle=1.5708
    g7: ArcOfCircle CenterX=-25.5 CenterY=38.6844 CenterZ=0 NormalX=0 NormalY=0 NormalZ=1 AngleXU=0 Radius=33.2344 StartAngle=4.71239 EndAngle=4.98193
    g8: LineSegment StartX=-25.5 StartY=9.95 StartZ=0 EndX=-25.5 EndY=5.45 EndZ=0
    g9: LineSegment StartX=-16.65 StartY=8.75 StartZ=0 EndX=-16.65 EndY=6.65 EndZ=0
  constraints (29):
    c: Vertical(g1)
    c: Coincident(g2,g1)
    c: Coincident(g3,g1)
    c: Coincident(g4,g2)
    c: Coincident(g4,g3)
    c: Vertical(g4)
    c: Distance(g1,g-1) = 8.75
    c: Distance(g1,g-1) = 6.65
    c: Distance(g1,g-2) = 16.65
    c: Distance(g3,g-2) = 25.5
    c: Diameter(g0) = 2
    c: Distance(g2,g3) = 4.5
    c: Perpendicular(g2,g4)
    c: Perpendicular(g3,g4)
    c: Distance(g0,g-1) = 7.7
    c: Distance(g3,g-1) = 5.45
    c: Symmetric(g5,g0,g-2)
    c: Diameter(g5) = 2
    c: Coincident(g8,g6)
    c: Coincident(g9,g6)
    c: Coincident(g9,g7)
    c: Symmetric(g6,g1,g-2)
    c: Symmetric(g7,g1,g-2)
    c: Coincident(g8,g7)
    c: Symmetric(g7,g3,g-2)
    c: Symmetric(g6,g2,g-2)
    c: Perpendicular(g6,g8)
    c: Perpendicular(g7,g8)
    c: Distance(g0,g4) = 3
FEATURE [Part::Extrusion] Extrude002  label="Con"
  Base = -> Sketch004
  Dir = (0,-1,-3e-16)
  DirMode = 2
  FaceMakerClass = Part::FaceMakerBullseye
  LengthFwd = 0.8
  LengthRev = 0
  Solid = true
  Symmetric = true
  expr: LengthFwd = <<DS>>.Con_Thickness
FEATURE [Part::Compound] Compound  label="Resistor Arcol HS"
  Links = -> [Fusion,Revolve,Revolve001,Extrude002]
